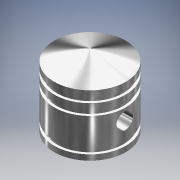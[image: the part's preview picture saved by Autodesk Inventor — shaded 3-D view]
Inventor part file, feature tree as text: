
AUTODESK INVENTOR PART (.ipt)
format: ipt  version: 2018.1 (Build 221171000, 171)  size: 221,696 bytes
history: native  units: in
note: dims shown in document units (in); Inventor stores cm internally (conversion verified against a paired STEP export)
features: sketch x3, extrude x2, revolve x1, plane x1, fillet x1
ambient origin geometry x8: Origin, YZ Plane, XZ Plane, XY Plane, X Axis, Y Axis, Z Axis, Center Point
bodies: Solid1 (feature_tree)
feature tree (8):
  revolve  "Revolution1"  Angle=90.0deg
  plane  "Work Plane1"
  extrude  "Extrusion1"  Depth=0.3543in TaperAngle=0.0deg
  fillet  "Fillet1"  Radius=0.0984in
  extrude  "Extrusion2"  [1 undecoded]
  sketch  "Sketch1"  dims[d4=0.2362in d11=90.0deg]
  sketch  "Sketch2"  dims[d12=0.0787in d17=0.3543in d18=0.0in d19=0.0984in]
  sketch  "Sketch3"  dims[d22=0.7874in d23=0.0in]
note: 1 required parameter value undecoded (feature->parameter linkage not recoverable at this tier; creation-order binding heuristic only, values carry confidence <= 0.55)
